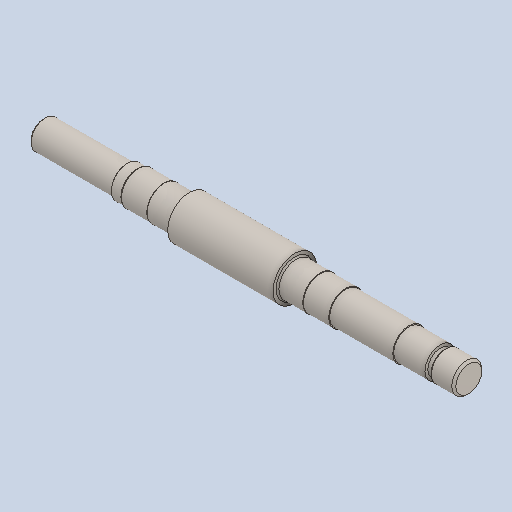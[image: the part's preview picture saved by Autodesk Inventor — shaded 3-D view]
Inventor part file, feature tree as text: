
AUTODESK INVENTOR PART (.ipt)
format: ipt  version: 2024.1 (Build 281209000, 209)  size: 146,944 bytes
history: native  units: in
note: dims shown in document units (in); Inventor stores cm internally (conversion verified against a paired STEP export)
features: chamfer x1
ambient origin geometry x8: Origin, YZ Plane, XZ Plane, XY Plane, X Axis, Y Axis, Z Axis, Center Point
bodies: Solid1 (feature_tree)
feature tree (1):
  chamfer  "Chamfer2"  [1 undecoded]
note: 1 required parameter value undecoded (feature->parameter linkage not recoverable at this tier; creation-order binding heuristic only, values carry confidence <= 0.55)
